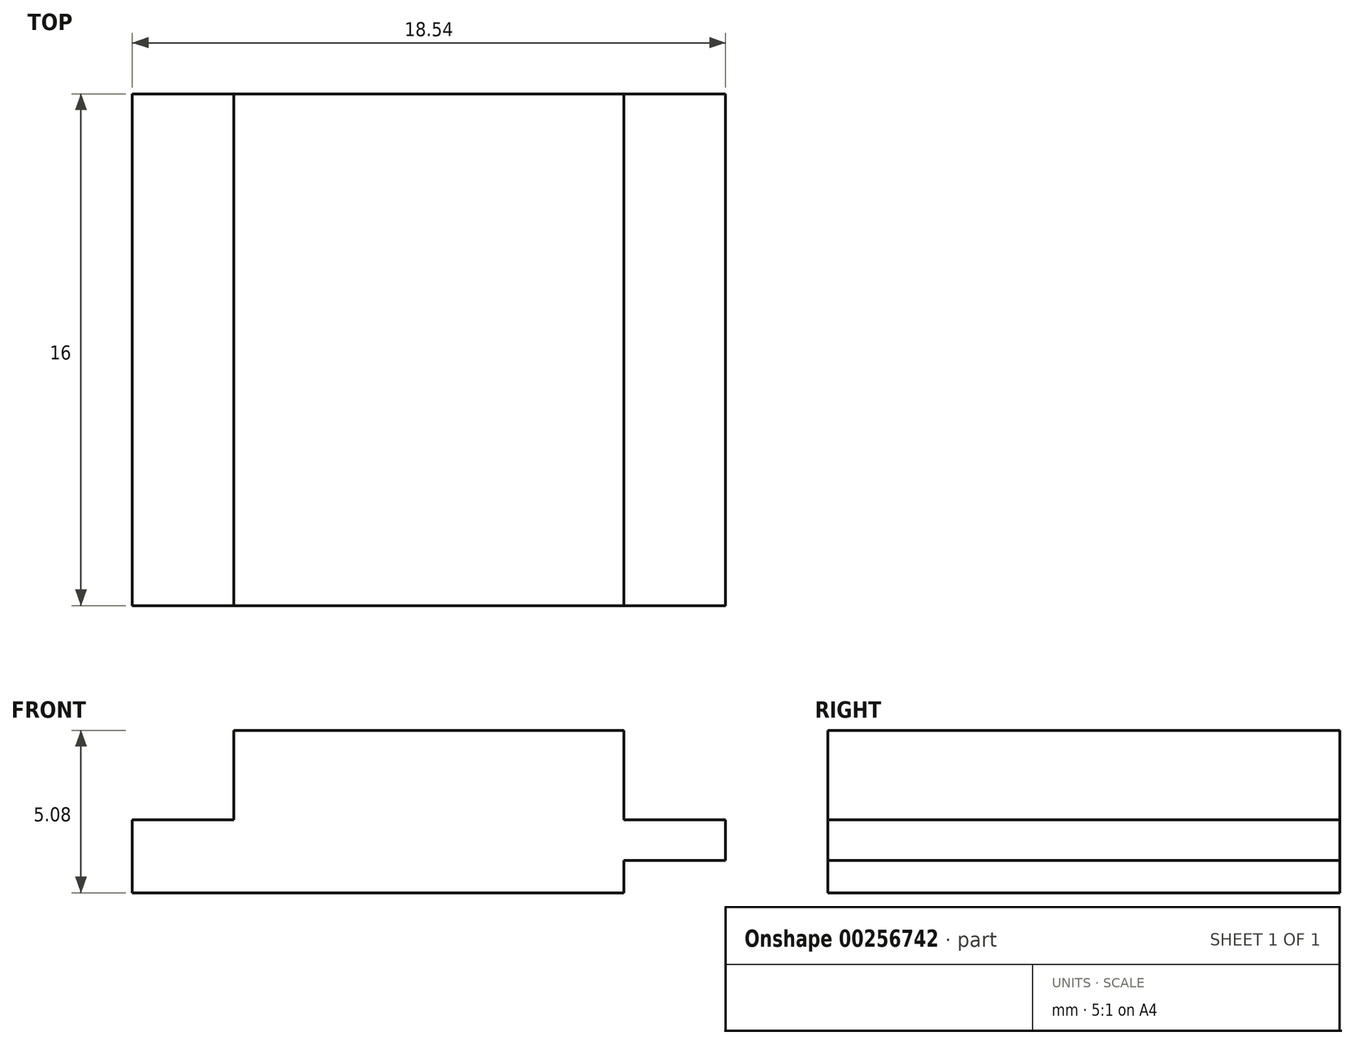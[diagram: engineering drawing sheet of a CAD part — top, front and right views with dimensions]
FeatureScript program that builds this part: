
annotation { "Feature Type Name" : "Feature", "Feature Type Description" : "" }
export const myFeature = defineFeature(function(context is Context, id is Id, definition is map)
    precondition{}
    {
        {
            var Q0;
            Q0=qCreatedBy(makeId("Front.planeOp"),FACE);
            var sketch = newSketch(context, id + "F0", { "sketchPlane" : qUnion([Q0])});
            skLineSegment(sketch, "E0", {"start": v(0, 0) * mm, "end": v(0, 2.29) * mm});
            skLineSegment(sketch, "E1", {"start": v(0, 2.29) * mm, "end": v(3.18, 2.29) * mm});
            skLineSegment(sketch, "E2", {"start": v(3.18, 2.29) * mm, "end": v(3.18, 5.08) * mm});
            skLineSegment(sketch, "E3", {"start": v(3.18, 5.08) * mm, "end": v(15.37, 5.08) * mm});
            skLineSegment(sketch, "E4", {"start": v(15.37, 5.08) * mm, "end": v(15.37, 2.29) * mm});
            skLineSegment(sketch, "E5", {"start": v(15.37, 2.29) * mm, "end": v(18.54, 2.29) * mm});
            skLineSegment(sketch, "E6", {"start": v(18.54, 1.02) * mm, "end": v(15.37, 1.02) * mm});
            skLineSegment(sketch, "E7", {"start": v(15.37, 1.02) * mm, "end": v(15.37, 0) * mm});
            skLineSegment(sketch, "E8", {"start": v(0, 0) * mm, "end": v(15.37, 0) * mm});
            skLineSegment(sketch, "E9", {"start": v(18.54, 2.29) * mm, "end": v(18.54, 1.02) * mm});
            skSolve(sketch);
        }
        {
            var Q0;
            Q0=makeQuery(id+"F0.imprint","IMPRINT",FACE,{"disambiguationData":[TD([[makeQuery(id+"F0.imprint","IMPRINT",EDGE,{"derivedFrom":sQuery(id+"F0.wireOp",EDGE,"E0")}),-1.0]])]});
            extrude(context, id + "F1", {"entities" : qUnion([Q0]), "oppositeDirection" : true, "depth" : 16 * mm});
        }
    });
